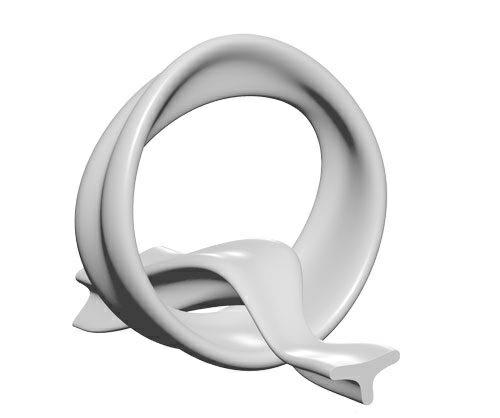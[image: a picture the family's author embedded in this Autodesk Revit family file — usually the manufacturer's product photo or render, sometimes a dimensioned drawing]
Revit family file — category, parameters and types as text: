
# Revit family: CITY ALPHABET litera „Q”
name_source: partatom
category: Meble
revit_build: Autodesk Revit 2018 (Build: 20190510_1515(x64)
units: mm (PartAtom-declared; Revit-internal decimal feet)

## family parameters
Numer OmniClass = 23.40.10.11.14
Obiekt nadrzędny = Powierzchnia
Punkt obliczania pomieszczeń = Nie
Tnij formami wycięć po wczytaniu = Nie
Tytuł OmniClass = Exterior Seating
Współdzielony = Nie

## types (1)
- CITY ALPHABET litera „Q"
    Domyślna rzędna = 1219 mm
    Długość = 2400 mm
    IfcExportAs = IfcFurnishingElement
    Komentarze do typu = Ławka
    Materiał - informacja = Szeroki wybór kolorów wg palety RAL. Istnieje również możliwość specjalnego wykonania
kolorystycznego na indywidualne zapytanie klienta.
    Model = CITY ALPHABET litera „Q”
    Obraz typu = Q.jpg
    Producent = Astrini Design
    Szerokość = 1850 mm  [stored 6.06955 ft]
    Temepratura użytkowania = -40°C do 80°C, ( -40°F do 176°F )
    URL = http://astrini-design.pl
    Waga (szacunkowo) = 95.00 kg
    Waga po wypełnieniu (szacunkowo) = 195.00 kg
    Wysokość = 1900 mm  [stored 6.2336 ft]

note: [stored X ft] marks values corroborated as IEEE doubles in the binary element streams (Revit-internal decimal feet)
